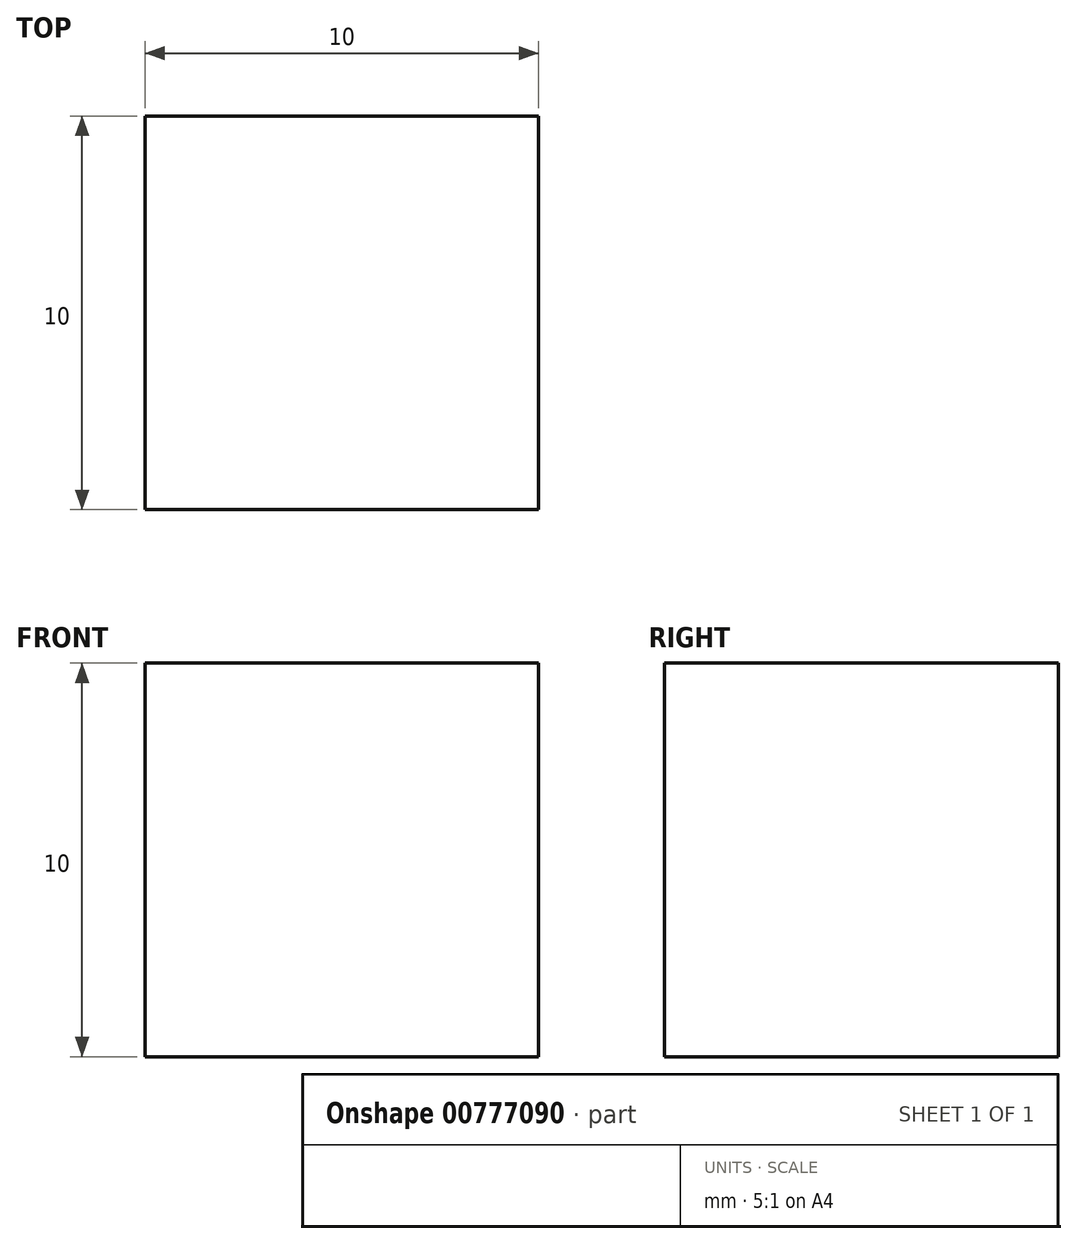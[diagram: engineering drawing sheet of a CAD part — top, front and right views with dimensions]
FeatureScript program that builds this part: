
annotation { "Feature Type Name" : "Feature", "Feature Type Description" : "" }
export const myFeature = defineFeature(function(context is Context, id is Id, definition is map)
    precondition{}
    {
        {
            var Q0;
            Q0=qCreatedBy(makeId("Top.planeOp"),FACE);
            var sketch = newSketch(context, id + "F0", { "sketchPlane" : qUnion([Q0])});
            skLineSegment(sketch, "E0.bottom", {"start": v(5, 5) * mm, "end": v(-5, 5) * mm});
            skLineSegment(sketch, "E0.top", {"start": v(5, -5) * mm, "end": v(-5, -5) * mm});
            skLineSegment(sketch, "E0.left", {"start": v(5, 5) * mm, "end": v(5, -5) * mm});
            skLineSegment(sketch, "E0.right", {"start": v(-5, 5) * mm, "end": v(-5, -5) * mm});
            skPoint(sketch, "E0.middle", {"position": v(0, 0) * mm});
            skSolve(sketch);
        }
        {
            var Q0;
            Q0=makeQuery(id+"F0.imprint","IMPRINT",FACE,{"disambiguationData":[TD([[makeQuery(id+"F0.imprint","IMPRINT",EDGE,{"derivedFrom":sQuery(id+"F0.wireOp",EDGE,"E0.bottom")}),1.0]])]});
            extrude(context, id + "F1", {"entities" : qUnion([Q0]), "depth" : 10 * mm, "offsetDistance" : 25 * mm});
        }
    });
